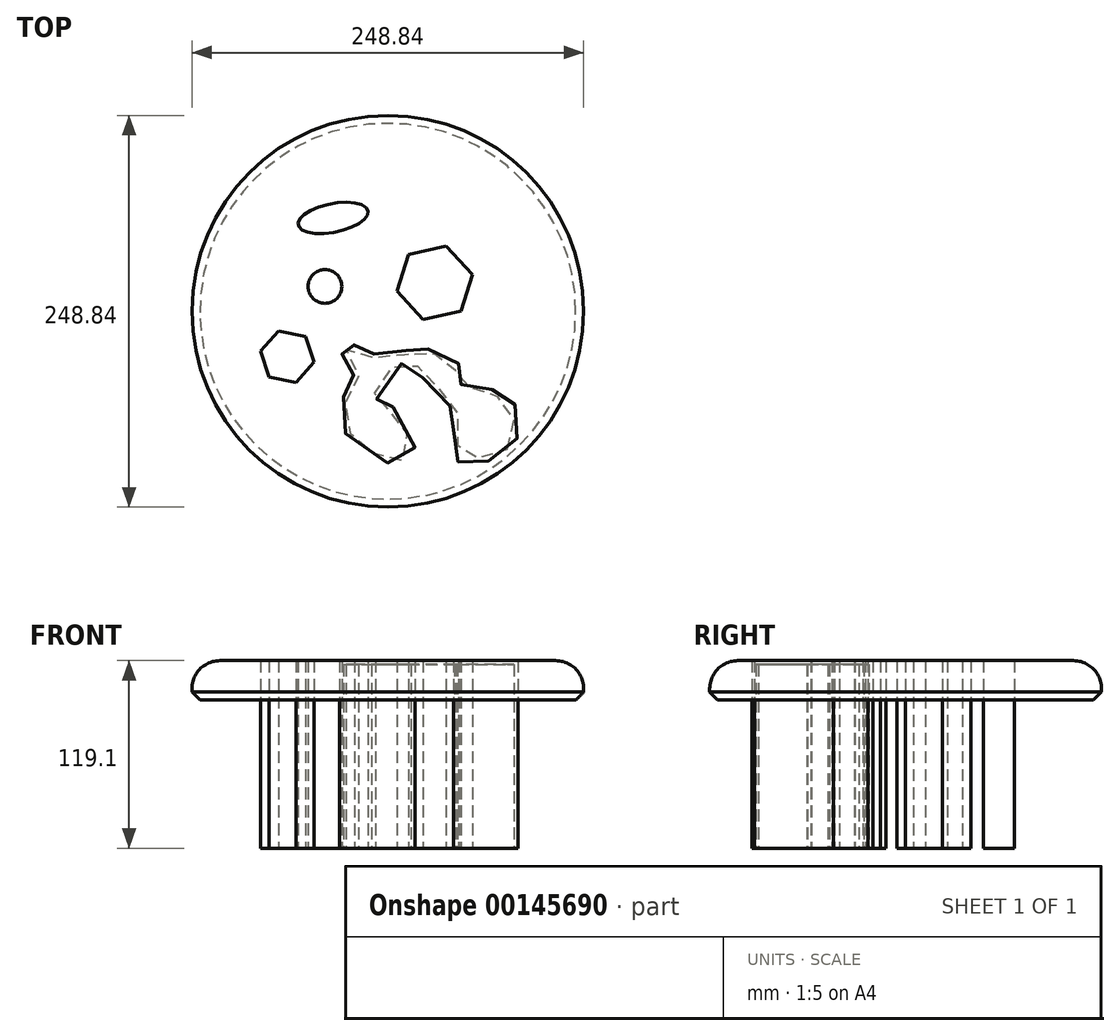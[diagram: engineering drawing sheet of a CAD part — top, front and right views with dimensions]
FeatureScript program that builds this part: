
annotation { "Feature Type Name" : "Feature", "Feature Type Description" : "" }
export const myFeature = defineFeature(function(context is Context, id is Id, definition is map)
    precondition{}
    {
        {
            var Q0;
            Q0=qCreatedBy(makeId("Top.planeOp"),FACE);
            var sketch = newSketch(context, id + "F0", { "sketchPlane" : qUnion([Q0])});
            skEllipse(sketch, "E0", {"center": v(-34.76, 59.3) * mm, "majorRadius": 22.61 * mm, "minorRadius": 9.06 * mm, "majorAxis": v(0.98, 0.2)});
            skCircle(sketch, "E1", {"center": v(-39.96, 15.77) * mm, "radius": 10.73 * mm});
            skPoint(sketch, "E1.first.point", {"position": v(-50.34, 13.02) * mm});
            skPoint(sketch, "E1.second.point", {"position": v(-37.21, 26.15) * mm});
            skPoint(sketch, "E1.third.point", {"position": v(-34.72, 6.4) * mm});
            skCircle(sketch, "E2.cCircle", {"center": v(29.7, 18.07) * mm, "radius": 21.28 * mm, "construction": true});
            skLineSegment(sketch, "E2.0", {"start": v(13.06, 36.14) * mm, "end": v(37.03, 41.53) * mm});
            skLineSegment(sketch, "E2.1", {"start": v(37.03, 41.53) * mm, "end": v(53.68, 23.45) * mm});
            skLineSegment(sketch, "E2.2", {"start": v(53.68, 23.45) * mm, "end": v(46.36, 0) * mm});
            skLineSegment(sketch, "E2.3", {"start": v(46.36, 0) * mm, "end": v(22.38, -5.38) * mm});
            skLineSegment(sketch, "E2.4", {"start": v(22.38, -5.38) * mm, "end": v(5.73, 12.69) * mm});
            skLineSegment(sketch, "E2.5", {"start": v(5.73, 12.69) * mm, "end": v(13.06, 36.14) * mm});
            skPoint(sketch, "E2.0.midPoint", {"position": v(25.05, 38.83) * mm});
            skCircle(sketch, "E3.cCircle", {"center": v(-63.85, -28.89) * mm, "radius": 17.34 * mm, "construction": true});
            skLineSegment(sketch, "E3.0", {"start": v(-69.34, -12.44) * mm, "end": v(-52.35, -15.91) * mm});
            skLineSegment(sketch, "E3.1", {"start": v(-52.35, -15.91) * mm, "end": v(-46.86, -32.37) * mm});
            skLineSegment(sketch, "E3.2", {"start": v(-46.86, -32.37) * mm, "end": v(-58.37, -45.34) * mm});
            skLineSegment(sketch, "E3.3", {"start": v(-58.37, -45.34) * mm, "end": v(-75.36, -41.87) * mm});
            skLineSegment(sketch, "E3.4", {"start": v(-75.36, -41.87) * mm, "end": v(-80.84, -25.41) * mm});
            skLineSegment(sketch, "E3.5", {"start": v(-80.84, -25.41) * mm, "end": v(-69.34, -12.44) * mm});
            skFitSpline(sketch, "E4", {"points": [v(-28.27, -54.35) * mm, v(-22.73, -83.16) * mm, v(15.5, -94.24) * mm, v(2.75, -60.72) * mm, v(-7.77, -59.34) * mm, v(9.13, -33.02) * mm, v(17.71, -37.45) * mm, v(39.6, -60.44) * mm, v(41.81, -67.1) * mm, v(43.2, -93.96) * mm, v(50.12, -95.9) * mm, v(77.82, -89.25) * mm, v(81.7, -61.83) * mm, v(76.71, -55.18) * mm, v(51.5, -45.76) * mm, v(45.13, -46.32) * mm, v(43.95, -31.18) * mm, v(22.14, -23.88) * mm, v(16.33, -24.43) * mm, v(-6.94, -26.93) * mm, v(-11.37, -26.37) * mm, v(-23.84, -20.83) * mm, v(-28.27, -23.33) * mm, v(-28, -32.47) * mm, v(-21.07, -42.44) * mm, v(-28.27, -54.35) * mm]});
            skSolve(sketch);
        }
        {
            var Q0;
            Q0 = qSketchRegion(id + "F0", true);
            extrude(context, id + "F1", {"entities" : qUnion([Q0]), "depth" : 119.1 * mm});
        }
        {
            var Q0;
            Q0=makeQuery(id+"F1.opExtrude","CAP_FACE",FACE,{"disambiguationData":[OSD([sQuery(id+"F0.wireOp",EDGE,"E2.0"),sQuery(id+"F0.wireOp",EDGE,"E2.1"),sQuery(id+"F0.wireOp",EDGE,"E2.2"),sQuery(id+"F0.wireOp",EDGE,"E2.3"),sQuery(id+"F0.wireOp",EDGE,"E2.4"),sQuery(id+"F0.wireOp",EDGE,"E2.5")])],"isStart":false});
            var sketch = newSketch(context, id + "F2", { "sketchPlane" : qUnion([Q0])});
            skCircle(sketch, "E5", {"center": v(0, 0) * mm, "radius": 124.42 * mm});
            skSolve(sketch);
        }
        {
            var Q0;
            Q0 = qSketchRegion(id + "F2", true);
            extrude(context, id + "F3", {"entities" : qUnion([Q0]), "oppositeDirection" : true, "depth" : 25.03 * mm});
        }
        {
            var Q0;
            Q0=makeQuery(id+"F3.opExtrude","CAP_EDGE",EDGE,{"disambiguationData":[OSD([sQuery(id+"F2.wireOp",EDGE,"E5")])],"isStart":false});
            chamfer(context, id + "F4", {"entities" : qUnion([Q0]), "width" : 5.08 * mm, "tangentPropagation" : true});
        }
        {
            var Q0;
            Q0=makeQuery(id+"F3.opExtrude","CAP_EDGE",EDGE,{"disambiguationData":[OSD([sQuery(id+"F2.wireOp",EDGE,"E5")])],"isStart":true});
            fillet(context, id + "F5", {"entities" : qUnion([Q0]), "radius" : 17.78 * mm, "tangentPropagation" : true, "allowEdgeOverflow" : false});
        }
        {
            var Q0;
            Q0=makeQuery(id+"F1.opExtrude","CAP_FACE",FACE,{"disambiguationData":[OSD([sQuery(id+"F0.wireOp",EDGE,"E4")])],"isStart":true});
            shell(context, id + "F6", {"entities" : qUnion([Q0]), "thickness" : 2.54 * mm});
        }
    });
